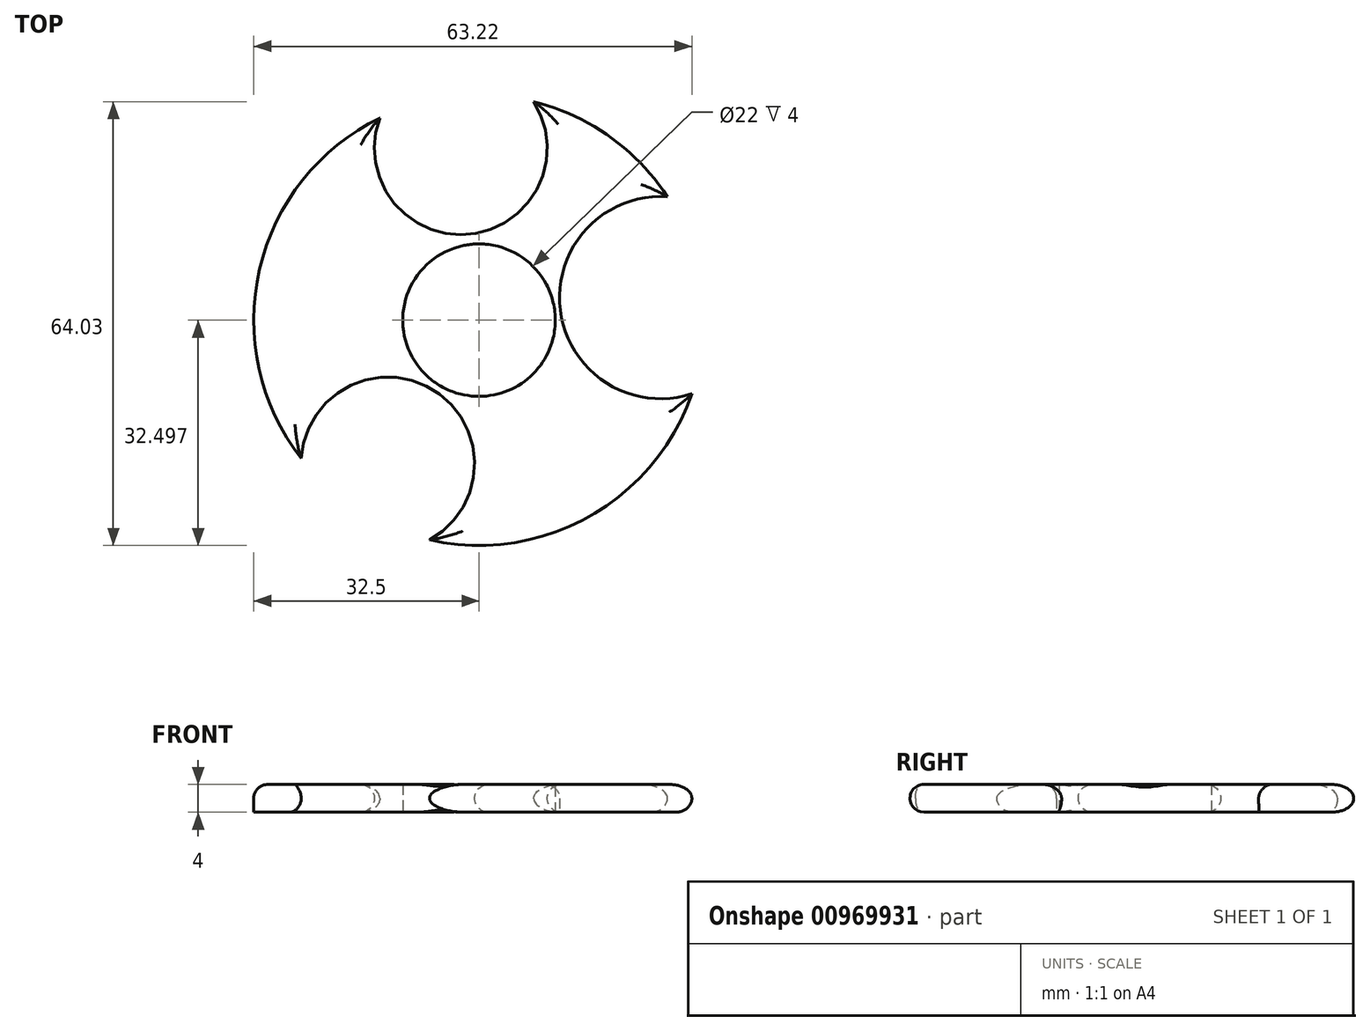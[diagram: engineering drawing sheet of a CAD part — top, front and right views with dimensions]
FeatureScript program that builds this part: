
annotation { "Feature Type Name" : "Feature", "Feature Type Description" : "" }
export const myFeature = defineFeature(function(context is Context, id is Id, definition is map)
    precondition{}
    {
        {
            var Q0;
            Q0=qCreatedBy(makeId("Top.planeOp"),FACE);
            var sketch = newSketch(context, id + "F0", { "sketchPlane" : qUnion([Q0])});
            skCircle(sketch, "E0", {"center": v(0, 18.16) * mm, "radius": 32.5 * mm});
            skCircle(sketch, "E1", {"center": v(0, 18.16) * mm, "radius": 11 * mm});
            skArc(sketch, "E2", {"start": v(-14.3, 47.34) * mm, "mid": v(-1.31, 30.57) * mm, "end": v(7.89, 49.69) * mm});
            skArc(sketch, "E3", {"start": v(27.19, 35.96) * mm, "mid": v(11.73, 19.61) * mm, "end": v(30.72, 7.54) * mm});
            skArc(sketch, "E4", {"start": v(-7.14, -13.55) * mm, "mid": v(-6.45, 8) * mm, "end": v(-25.66, -1.8) * mm});
            skSolve(sketch);
        }
        {
            var Q0;
            Q0=makeQuery(id+"F0.imprint","IMPRINT",FACE,{"disambiguationData":[TD([[makeQuery(id+"F0.imprint","IMPRINT",EDGE,{"derivedFrom":sQuery(id+"F0.wireOp",EDGE,"E0")}),1.0]])]});
            extrude(context, id + "F1", {"entities" : qUnion([Q0]), "depth" : 2 * mm, "offsetDistance" : 25 * mm});
        }
        {
            var Q0;
            Q0=makeQuery(id+"F1.opExtrude","CAP_FACE",FACE,{"disambiguationData":[OSD([sQuery(id+"F0.wireOp",EDGE,"E0"),sQuery(id+"F0.wireOp",EDGE,"E1"),sQuery(id+"F0.wireOp",EDGE,"E2"),sQuery(id+"F0.wireOp",EDGE,"E3"),sQuery(id+"F0.wireOp",EDGE,"E4")])],"isStart":false});
            extrude(context, id + "F2", {"entities" : qUnion([Q0]), "operationType" : NewBodyOperationType.ADD, "depth" : 2 * mm, "offsetDistance" : 25 * mm});
        }
        {
            var Q0;
            {var subQ0=sQuery(id+"F0.wireOp",EDGE,"E2");Q0=makeQuery(id+"F0.imprint","IMPRINT",FACE,{"disambiguationData":[TD([[makeQuery(id+"F0.imprint","IMPRINT",EDGE,{"derivedFrom":subQ0}),1.0]])]});}
            var Q1;
            {var subQ0=sQuery(id+"F0.wireOp",EDGE,"E3");Q1=makeQuery(id+"F0.imprint","IMPRINT",FACE,{"disambiguationData":[TD([[makeQuery(id+"F0.imprint","IMPRINT",EDGE,{"derivedFrom":subQ0}),1.0]])]});}
            var Q2;
            {var subQ0=sQuery(id+"F0.wireOp",EDGE,"E4");Q2=makeQuery(id+"F0.imprint","IMPRINT",FACE,{"disambiguationData":[TD([[makeQuery(id+"F0.imprint","IMPRINT",EDGE,{"derivedFrom":subQ0}),1.0]])]});}
            extrude(context, id + "F3", {"entities" : qUnion([Q0, Q1, Q2]), "operationType" : NewBodyOperationType.REMOVE, "oppositeDirection" : true, "depth" : 25 * mm, "offsetDistance" : 25 * mm});
        }
        {
            var Q0;
            {var subQ0=sQuery(id+"F0.wireOp",EDGE,"E0");Q0=makeQuery(id+"F2.opExtrude","CAP_EDGE",EDGE,{"disambiguationData":[OSD([subQ0]),TDD([makeQuery(id+"F1.opExtrude","CAP_EDGE",EDGE,{"disambiguationData":[OSD([subQ0]),TDD([makeQuery(id+"F0.imprint","IMPRINT",EDGE,{"disambiguationData":[TD([[makeQuery(id+"F0.imprint","INTERSECT",VERTEX,{"disambiguationData":[OD(0.0)],"derivedFrom":[subQ0,sQuery(id+"F0.wireOp",EDGE,"E2")]}),-1.0]])],"derivedFrom":subQ0})])],"isStart":false})])],"isStart":false});}
            var Q1;
            Q1=makeQuery(id+"F2.opExtrude","CAP_EDGE",EDGE,{"disambiguationData":[OSD([sQuery(id+"F0.wireOp",EDGE,"E4")])],"isStart":false});
            var Q2;
            {var subQ0=sQuery(id+"F0.wireOp",EDGE,"E0");Q2=makeQuery(id+"F2.opExtrude","CAP_EDGE",EDGE,{"disambiguationData":[OSD([subQ0]),TDD([makeQuery(id+"F1.opExtrude","CAP_EDGE",EDGE,{"disambiguationData":[OSD([subQ0]),TDD([makeQuery(id+"F0.imprint","IMPRINT",EDGE,{"disambiguationData":[TD([[makeQuery(id+"F0.imprint","INTERSECT",VERTEX,{"disambiguationData":[OD(1.0)],"derivedFrom":[subQ0,sQuery(id+"F0.wireOp",EDGE,"E3")]}),1.0]])],"derivedFrom":subQ0})])],"isStart":false})])],"isStart":false});}
            var Q3;
            Q3=makeQuery(id+"F2.opExtrude","CAP_EDGE",EDGE,{"disambiguationData":[OSD([sQuery(id+"F0.wireOp",EDGE,"E3")])],"isStart":false});
            var Q4;
            {var subQ0=sQuery(id+"F0.wireOp",EDGE,"E0");Q4=makeQuery(id+"F1.opExtrude","CAP_EDGE",EDGE,{"disambiguationData":[OSD([subQ0]),TDD([makeQuery(id+"F0.imprint","IMPRINT",EDGE,{"disambiguationData":[TD([[makeQuery(id+"F0.imprint","INTERSECT",VERTEX,{"disambiguationData":[OD(1.0)],"derivedFrom":[subQ0,sQuery(id+"F0.wireOp",EDGE,"E2")]}),1.0]])],"derivedFrom":subQ0})])],"isStart":true});}
            var Q5;
            Q5=makeQuery(id+"F2.opExtrude","CAP_EDGE",EDGE,{"disambiguationData":[OSD([sQuery(id+"F0.wireOp",EDGE,"E2")])],"isStart":false});
            var Q6;
            {var subQ0=sQuery(id+"F0.wireOp",EDGE,"E0");Q6=makeQuery(id+"F2.opExtrude","CAP_EDGE",EDGE,{"disambiguationData":[OSD([subQ0]),TDD([makeQuery(id+"F1.opExtrude","CAP_EDGE",EDGE,{"disambiguationData":[OSD([subQ0]),TDD([makeQuery(id+"F0.imprint","IMPRINT",EDGE,{"disambiguationData":[TD([[makeQuery(id+"F0.imprint","INTERSECT",VERTEX,{"disambiguationData":[OD(1.0)],"derivedFrom":[subQ0,sQuery(id+"F0.wireOp",EDGE,"E2")]}),1.0]])],"derivedFrom":subQ0})])],"isStart":false})])],"isStart":false});}
            var Q7;
            Q7=makeQuery(id+"F1.opExtrude","CAP_EDGE",EDGE,{"disambiguationData":[OSD([sQuery(id+"F0.wireOp",EDGE,"E2")])],"isStart":true});
            var Q8;
            Q8=makeQuery(id+"F1.opExtrude","CAP_EDGE",EDGE,{"disambiguationData":[OSD([sQuery(id+"F0.wireOp",EDGE,"E4")])],"isStart":true});
            var Q9;
            {var subQ0=sQuery(id+"F0.wireOp",EDGE,"E0");Q9=makeQuery(id+"F1.opExtrude","CAP_EDGE",EDGE,{"disambiguationData":[OSD([subQ0]),TDD([makeQuery(id+"F0.imprint","IMPRINT",EDGE,{"disambiguationData":[TD([[makeQuery(id+"F0.imprint","INTERSECT",VERTEX,{"disambiguationData":[OD(1.0)],"derivedFrom":[subQ0,sQuery(id+"F0.wireOp",EDGE,"E3")]}),1.0]])],"derivedFrom":subQ0})])],"isStart":true});}
            fillet(context, id + "F4", {"entities" : qUnion([Q0, Q1, Q2, Q3, Q4, Q5, Q6, Q7, Q8, Q9]), "radius" : 2 * mm, "tangentPropagation" : true, "allowEdgeOverflow" : false});
        }
    });
